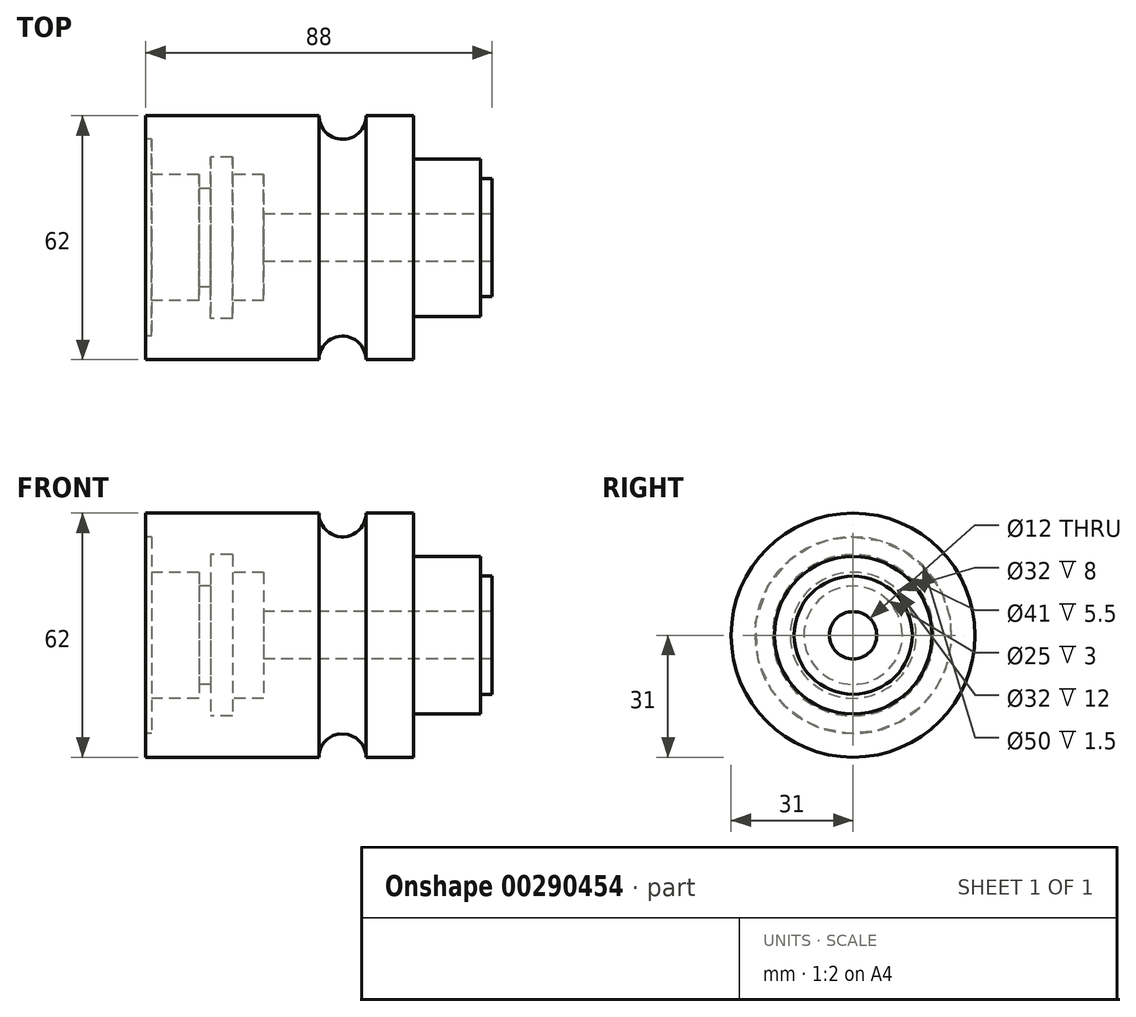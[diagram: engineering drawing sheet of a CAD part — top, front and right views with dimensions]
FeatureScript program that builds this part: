
annotation { "Feature Type Name" : "Feature", "Feature Type Description" : "" }
export const myFeature = defineFeature(function(context is Context, id is Id, definition is map)
    precondition{}
    {
        {
            var Q0;
            Q0=qCreatedBy(makeId("Front.planeOp"),FACE);
            var sketch = newSketch(context, id + "F0", { "sketchPlane" : qUnion([Q0])});
            skLineSegment(sketch, "E0", {"start": v(0, 0) * mm, "end": v(109.05, 0) * mm, "construction": true});
            skLineSegment(sketch, "E1", {"start": v(0, 0) * mm, "end": v(0, 31) * mm});
            skLineSegment(sketch, "E2", {"start": v(0, 31) * mm, "end": v(44, 31) * mm});
            skLineSegment(sketch, "E3", {"start": v(68, 31) * mm, "end": v(68, 20) * mm});
            skLineSegment(sketch, "E4", {"start": v(68, 20) * mm, "end": v(85, 20) * mm});
            skLineSegment(sketch, "E5", {"start": v(85, 20) * mm, "end": v(85, 15) * mm});
            skLineSegment(sketch, "E6", {"start": v(85, 15) * mm, "end": v(88, 15) * mm});
            skLineSegment(sketch, "E7", {"start": v(88, 15) * mm, "end": v(88, 0) * mm});
            skLineSegment(sketch, "E8", {"start": v(0, 0) * mm, "end": v(88, 0) * mm});
            skArc(sketch, "E9", {"start": v(44, 31) * mm, "mid": v(50, 25) * mm, "end": v(56, 31) * mm});
            skLineSegment(sketch, "E10.trimOffspring", {"start": v(56, 31) * mm, "end": v(68, 31) * mm});
            skSolve(sketch);
        }
        {
            var Q0;
            Q0 = qSketchRegion(id + "F0", true);
            var Q1;
            Q1=sQuery(id+"F0.wireOp",EDGE,"E0");
            revolve(context, id + "F1", {"entities" : qUnion([Q0]), "axis" : qUnion([Q1]), "revolveType" : RevolveType.FULL});
        }
        {
            var Q0;
            Q0=qCreatedBy(makeId("Front.planeOp"),FACE);
            var sketch = newSketch(context, id + "F2", { "sketchPlane" : qUnion([Q0])});
            skLineSegment(sketch, "E11", {"start": v(0, 0) * mm, "end": v(0, 25) * mm});
            skLineSegment(sketch, "E12", {"start": v(0, 25) * mm, "end": v(1.5, 25) * mm});
            skLineSegment(sketch, "E13", {"start": v(1.5, 25) * mm, "end": v(1.5, 16) * mm});
            skLineSegment(sketch, "E14", {"start": v(1.5, 16) * mm, "end": v(13.5, 16) * mm});
            skLineSegment(sketch, "E15", {"start": v(13.5, 16) * mm, "end": v(13.5, 12.5) * mm});
            skLineSegment(sketch, "E16", {"start": v(13.5, 12.5) * mm, "end": v(16.5, 12.5) * mm});
            skLineSegment(sketch, "E17", {"start": v(16.5, 12.5) * mm, "end": v(16.5, 20.5) * mm});
            skLineSegment(sketch, "E18", {"start": v(16.5, 20.5) * mm, "end": v(22, 20.5) * mm});
            skLineSegment(sketch, "E19", {"start": v(22, 20.5) * mm, "end": v(22, 16) * mm});
            skLineSegment(sketch, "E20", {"start": v(22, 16) * mm, "end": v(30, 16) * mm});
            skLineSegment(sketch, "E21", {"start": v(30, 16) * mm, "end": v(30, 6) * mm});
            skLineSegment(sketch, "E22", {"start": v(30, 6) * mm, "end": v(135.94, 6) * mm});
            skLineSegment(sketch, "E23", {"start": v(135.94, 6) * mm, "end": v(135.94, 0) * mm});
            skLineSegment(sketch, "E24", {"start": v(135.94, 0) * mm, "end": v(0, 0) * mm});
            skLineSegment(sketch, "E25", {"start": v(0, 0) * mm, "end": v(-39.36, 0) * mm, "construction": true});
            skSolve(sketch);
        }
        {
            var Q0;
            Q0 = qSketchRegion(id + "F2", true);
            var Q1;
            Q1=sQuery(id+"F2.wireOp",EDGE,"E25");
            revolve(context, id + "F3", {"operationType" : NewBodyOperationType.REMOVE, "entities" : qUnion([Q0]), "axis" : qUnion([Q1]), "revolveType" : RevolveType.FULL, "oppositeDirection" : true});
        }
    });
